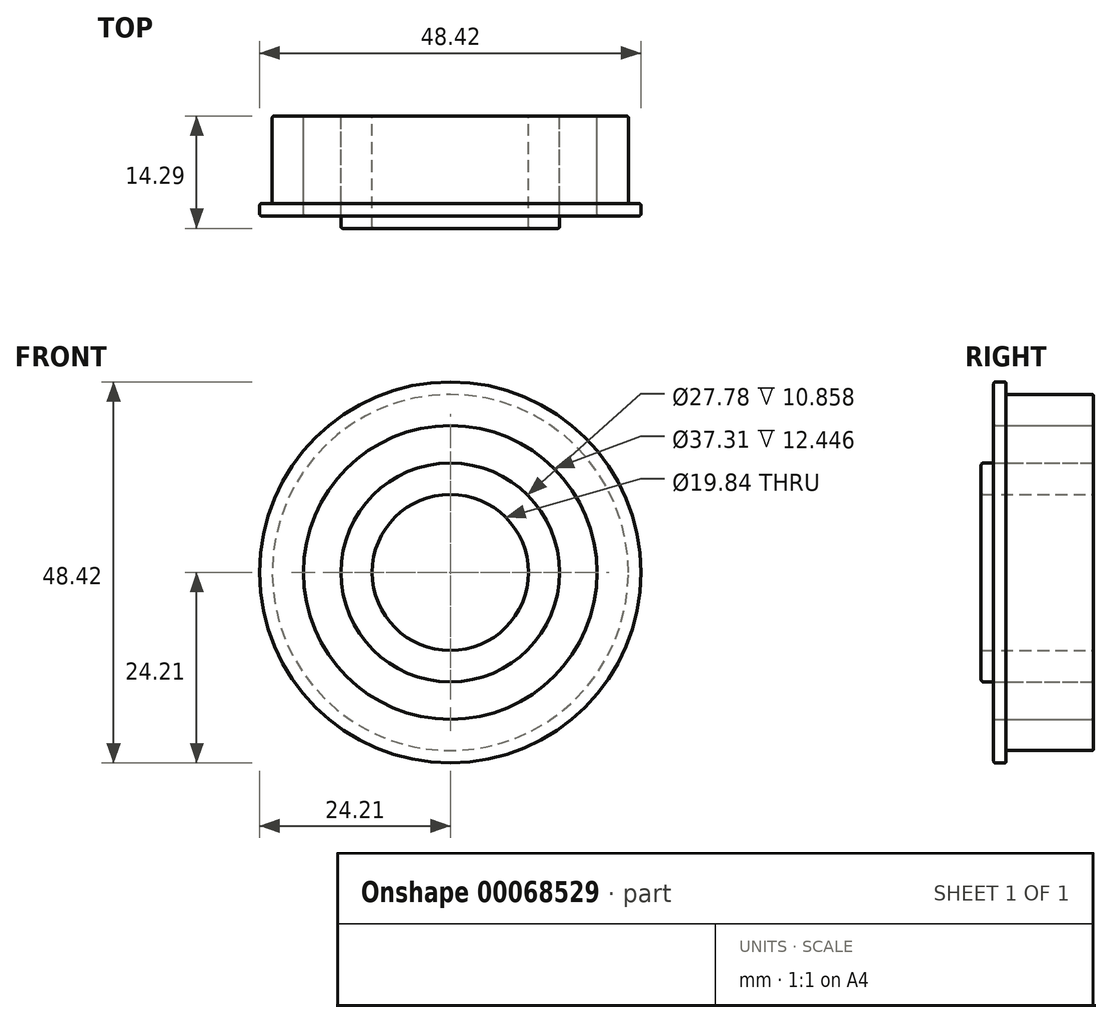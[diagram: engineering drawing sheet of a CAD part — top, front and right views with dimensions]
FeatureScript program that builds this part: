
annotation { "Feature Type Name" : "Feature", "Feature Type Description" : "" }
export const myFeature = defineFeature(function(context is Context, id is Id, definition is map)
    precondition{}
    {
        {
            var Q0;
            Q0=qCreatedBy(makeId("Front.planeOp"),FACE);
            var sketch = newSketch(context, id + "F0", { "sketchPlane" : qUnion([Q0])});
            skCircle(sketch, "E0", {"center": v(0, 0) * mm, "radius": 9.92 * mm});
            skCircle(sketch, "E1", {"center": v(0, 0) * mm, "radius": 13.9 * mm});
            skCircle(sketch, "E2", {"center": v(0, 0) * mm, "radius": 18.65 * mm});
            skCircle(sketch, "E3", {"center": v(0, 0) * mm, "radius": 24.2 * mm});
            skCircle(sketch, "E4", {"center": v(0, 0) * mm, "radius": 22.62 * mm});
            skSolve(sketch);
        }
        {
            var Q0;
            Q0=makeQuery(id+"F0.imprint","IMPRINT",FACE,{"disambiguationData":[TD([[makeQuery(id+"F0.imprint","IMPRINT",EDGE,{"derivedFrom":sQuery(id+"F0.wireOp",EDGE,"E0")}),-1.0]])]});
            extrude(context, id + "F1", {"entities" : qUnion([Q0]), "depth" : 14.29 * mm});
        }
        {
            var Q0;
            Q0=makeQuery(id+"F0.imprint","IMPRINT",FACE,{"disambiguationData":[TD([[makeQuery(id+"F0.imprint","IMPRINT",EDGE,{"derivedFrom":sQuery(id+"F0.wireOp",EDGE,"E1")}),-1.0]])]});
            extrude(context, id + "F2", {"entities" : qUnion([Q0]), "depth" : 11.1 * mm});
        }
        {
            var Q0;
            Q0=makeQuery(id+"F0.imprint","IMPRINT",FACE,{"disambiguationData":[TD([[makeQuery(id+"F0.imprint","IMPRINT",EDGE,{"derivedFrom":sQuery(id+"F0.wireOp",EDGE,"E2")}),-1.0]])]});
            extrude(context, id + "F3", {"entities" : qUnion([Q0]), "depth" : 12.7 * mm});
        }
        {
            var Q0;
            Q0=makeQuery(id+"F3.opExtrude","CAP_FACE",FACE,{"disambiguationData":[OSD([sQuery(id+"F0.wireOp",EDGE,"E2"),sQuery(id+"F0.wireOp",EDGE,"E4")])],"isStart":false});
            var sketch = newSketch(context, id + "F4", { "sketchPlane" : qUnion([Q0])});
            skCircle(sketch, "E5.0", {"center": v(0, 0) * mm, "radius": 24.2 * mm});
            skSolve(sketch);
        }
        {
            var Q0;
            Q0=makeQuery(id+"F4.imprint","IMPRINT",FACE,{"disambiguationData":[TD([[makeQuery(id+"F4.imprint","IMPRINT",EDGE,{"derivedFrom":sQuery(id+"F4.wireOp",EDGE,"E5.0")}),1.0]])]});
            extrude(context, id + "F5", {"entities" : qUnion([Q0]), "operationType" : NewBodyOperationType.ADD, "oppositeDirection" : true, "depth" : 1.59 * mm});
        }
        {
            var Q0;
            Q0=makeQuery(id+"F5.opExtrude","CAP_EDGE",EDGE,{"disambiguationData":[OSD([sQuery(id+"F4.wireOp",EDGE,"E5.0")])],"isStart":false});
            var Q1;
            Q1=makeQuery(id+"F5.opExtrude","CAP_EDGE",EDGE,{"disambiguationData":[OSD([sQuery(id+"F4.wireOp",EDGE,"E5.0")])],"isStart":true});
            var Q2;
            Q2=makeQuery(id+"F3.opExtrude","CAP_EDGE",EDGE,{"disambiguationData":[OSD([sQuery(id+"F0.wireOp",EDGE,"E2")])],"isStart":false});
            var Q3;
            Q3=makeQuery(id+"F2.opExtrude","CAP_EDGE",EDGE,{"disambiguationData":[OSD([sQuery(id+"F0.wireOp",EDGE,"E1")])],"isStart":false});
            var Q4;
            Q4=makeQuery(id+"F1.opExtrude","CAP_EDGE",EDGE,{"disambiguationData":[OSD([sQuery(id+"F0.wireOp",EDGE,"E1")])],"isStart":false});
            var Q5;
            Q5=makeQuery(id+"F1.opExtrude","CAP_EDGE",EDGE,{"disambiguationData":[OSD([sQuery(id+"F0.wireOp",EDGE,"E0")])],"isStart":false});
            var Q6;
            Q6=makeQuery(id+"F3.opExtrude","CAP_EDGE",EDGE,{"disambiguationData":[OSD([sQuery(id+"F0.wireOp",EDGE,"E4")])],"isStart":true});
            var Q7;
            Q7=makeQuery(id+"F2.opExtrude","CAP_EDGE",EDGE,{"disambiguationData":[OSD([sQuery(id+"F0.wireOp",EDGE,"E2")])],"isStart":true});
            var Q8;
            Q8=makeQuery(id+"F1.opExtrude","CAP_EDGE",EDGE,{"disambiguationData":[OSD([sQuery(id+"F0.wireOp",EDGE,"E1")])],"isStart":true});
            var Q9;
            Q9=makeQuery(id+"F1.opExtrude","CAP_EDGE",EDGE,{"disambiguationData":[OSD([sQuery(id+"F0.wireOp",EDGE,"E0")])],"isStart":true});
            fillet(context, id + "F6", {"entities" : qUnion([Q0, Q1, Q2, Q3, Q4, Q5, Q6, Q7, Q8, Q9]), "radius" : 0.25 * mm, "tangentPropagation" : true, "allowEdgeOverflow" : false});
        }
    });
